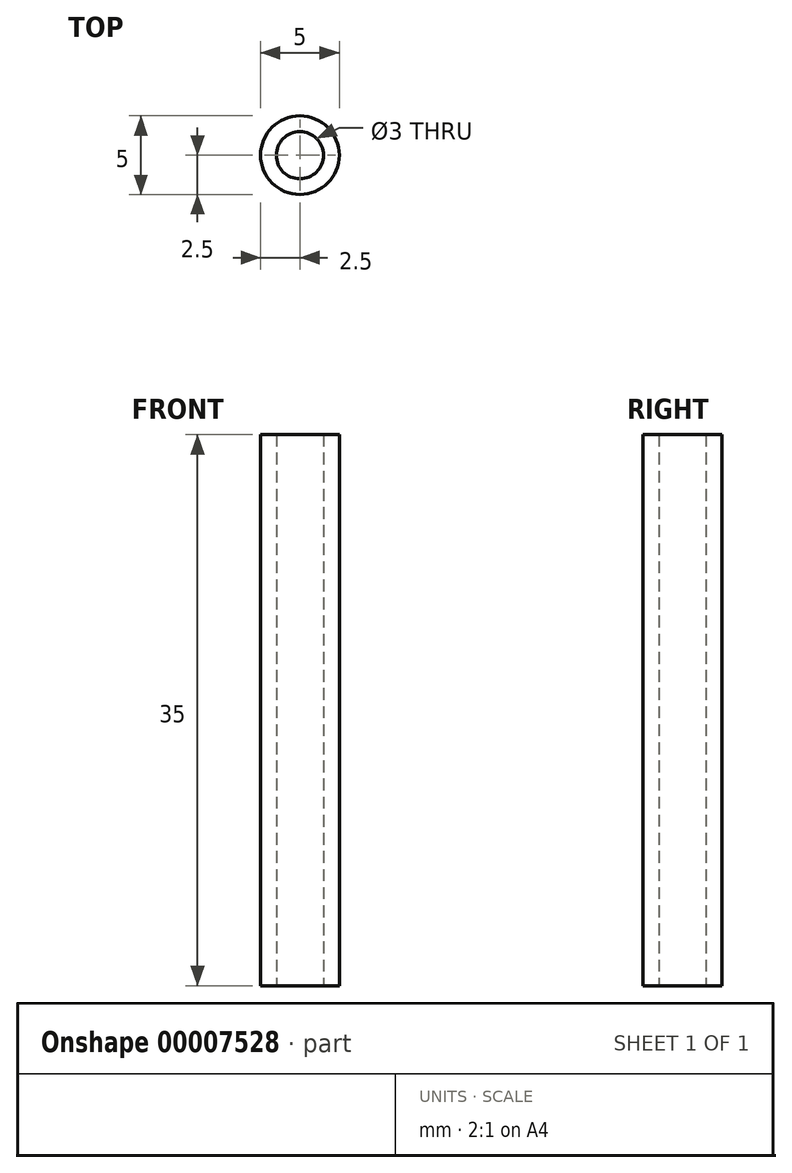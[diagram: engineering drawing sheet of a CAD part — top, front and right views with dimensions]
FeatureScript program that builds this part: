
annotation { "Feature Type Name" : "Feature", "Feature Type Description" : "" }
export const myFeature = defineFeature(function(context is Context, id is Id, definition is map)
    precondition{}
    {
        {
            var Q0;
            Q0=qCreatedBy(makeId("Top.planeOp"),FACE);
            var sketch = newSketch(context, id + "F0", { "sketchPlane" : qUnion([Q0])});
            skCircle(sketch, "E0", {"center": v(0, 0) * mm, "radius": 2.5 * mm});
            skCircle(sketch, "E1", {"center": v(0, 0) * mm, "radius": 1.5 * mm});
            skSolve(sketch);
        }
        {
            var Q0;
            Q0=makeQuery(id+"F0.imprint","IMPRINT",FACE,{"disambiguationData":[TD([[makeQuery(id+"F0.imprint","IMPRINT",EDGE,{"derivedFrom":sQuery(id+"F0.wireOp",EDGE,"E0")}),1.0]])]});
            extrude(context, id + "F1", {"entities" : qUnion([Q0]), "depth" : 35 * mm, "offsetDistance" : 25 * mm});
        }
    });
